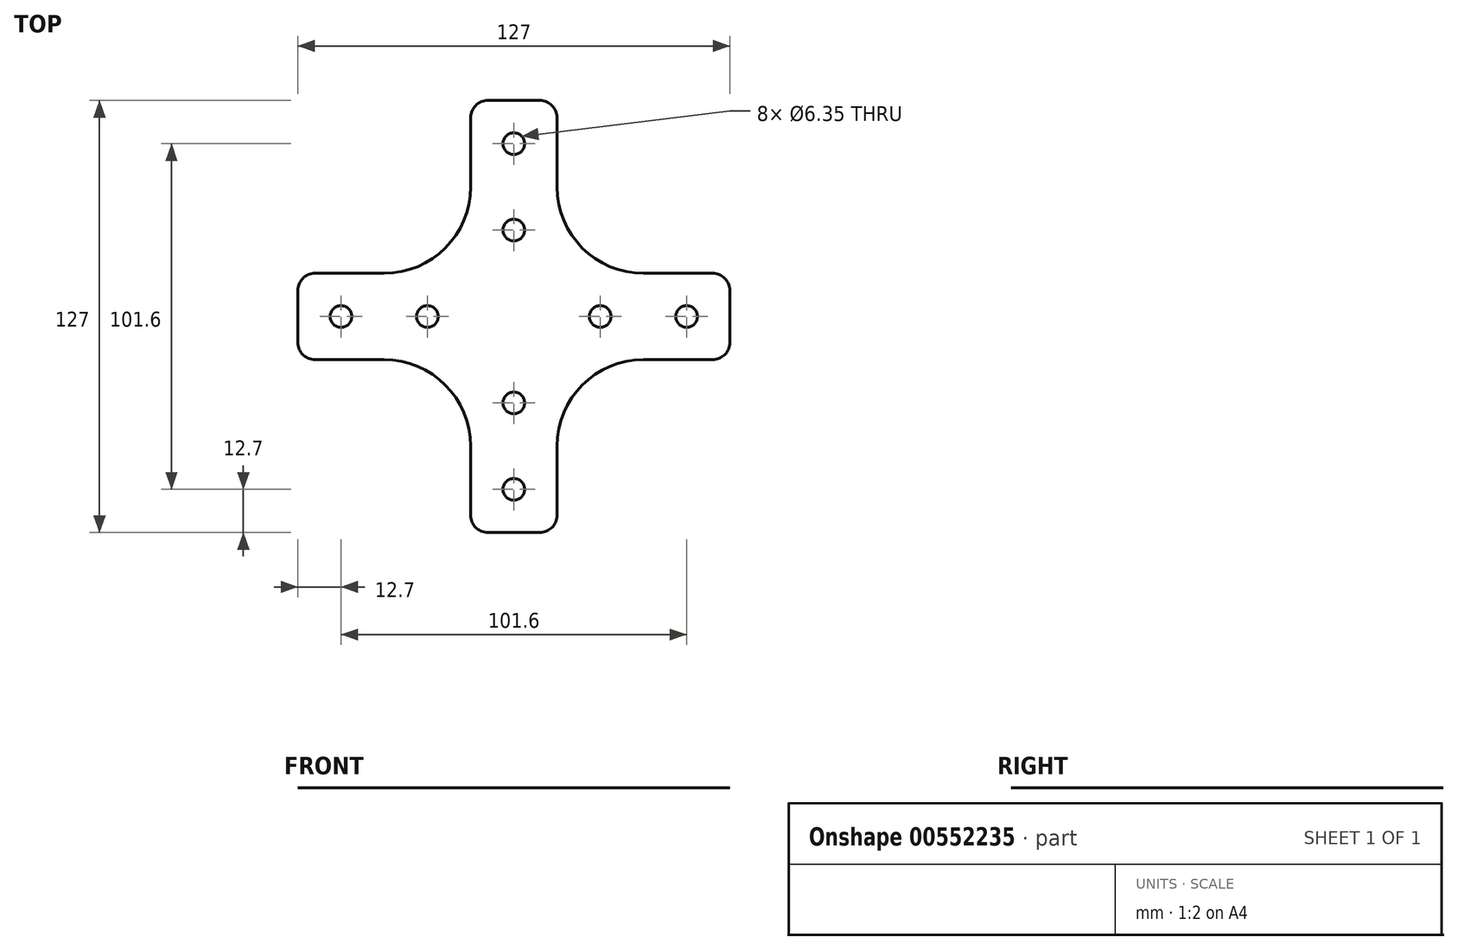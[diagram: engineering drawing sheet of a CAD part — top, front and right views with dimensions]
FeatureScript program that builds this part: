
annotation { "Feature Type Name" : "Feature", "Feature Type Description" : "" }
export const myFeature = defineFeature(function(context is Context, id is Id, definition is map)
    precondition{}
    {
        {
            var Q0;
            Q0=qCreatedBy(makeId("Top.planeOp"),FACE);
            var sketch = newSketch(context, id + "F0", { "sketchPlane" : qUnion([Q0])});
            skPoint(sketch, "E0.middle", {"position": v(0, 0) * mm});
            skLineSegment(sketch, "E1.bottom", {"start": v(-58.42, -12.7) * mm, "end": v(-38.1, -12.7) * mm});
            skLineSegment(sketch, "E1.top", {"start": v(-58.42, 12.7) * mm, "end": v(-38.1, 12.7) * mm});
            skLineSegment(sketch, "E2.left", {"start": v(-12.7, -58.42) * mm, "end": v(-12.7, -38.1) * mm});
            skLineSegment(sketch, "E2.right", {"start": v(12.7, -58.42) * mm, "end": v(12.7, -38.1) * mm});
            skLineSegment(sketch, "E3", {"start": v(38.1, -12.7) * mm, "end": v(58.42, -12.7) * mm});
            skLineSegment(sketch, "E4.bottom", {"start": v(-7.62, 63.5) * mm, "end": v(7.62, 63.5) * mm});
            skLineSegment(sketch, "E4.left", {"start": v(-12.7, 58.42) * mm, "end": v(-12.7, 38.1) * mm});
            skLineSegment(sketch, "E4.right", {"start": v(12.7, 58.42) * mm, "end": v(12.7, 38.1) * mm});
            skLineSegment(sketch, "E5.top", {"start": v(58.42, 12.7) * mm, "end": v(38.1, 12.7) * mm});
            skLineSegment(sketch, "E6.left", {"start": v(-63.5, 7.62) * mm, "end": v(-63.5, 0) * mm});
            skLineSegment(sketch, "E7.top", {"start": v(0, -63.5) * mm, "end": v(-7.62, -63.5) * mm});
            skLineSegment(sketch, "E8.right", {"start": v(63.5, 0) * mm, "end": v(63.5, -7.62) * mm});
            skCircle(sketch, "E9", {"center": v(-50.8, 0) * mm, "radius": 3.18 * mm});
            skCircle(sketch, "E10", {"center": v(-25.4, 0) * mm, "radius": 3.18 * mm});
            skCircle(sketch, "E11", {"center": v(0, -50.8) * mm, "radius": 3.18 * mm});
            skCircle(sketch, "E12", {"center": v(0, -25.4) * mm, "radius": 3.18 * mm});
            skCircle(sketch, "E13", {"center": v(50.8, 0) * mm, "radius": 3.18 * mm});
            skCircle(sketch, "E14", {"center": v(25.4, 0) * mm, "radius": 3.18 * mm});
            skCircle(sketch, "E15", {"center": v(0, 50.8) * mm, "radius": 3.18 * mm});
            skCircle(sketch, "E16", {"center": v(0, 25.4) * mm, "radius": 3.18 * mm});
            skArc(sketch, "E17.filletArc", {"start": v(-12.7, -38.1) * mm, "mid": v(-20.14, -20.14) * mm, "end": v(-38.1, -12.7) * mm});
            skArc(sketch, "E18.filletArc", {"start": v(38.1, -12.7) * mm, "mid": v(20.14, -20.14) * mm, "end": v(12.7, -38.1) * mm});
            skArc(sketch, "E19.filletArc", {"start": v(12.7, 38.1) * mm, "mid": v(20.14, 20.14) * mm, "end": v(38.1, 12.7) * mm});
            skArc(sketch, "E20.filletArc", {"start": v(-38.1, 12.7) * mm, "mid": v(-20.14, 20.14) * mm, "end": v(-12.7, 38.1) * mm});
            skArc(sketch, "E21.filletArc", {"start": v(-63.5, -7.62) * mm, "mid": v(-62.01, -11.21) * mm, "end": v(-58.42, -12.7) * mm});
            skArc(sketch, "E22.filletArc", {"start": v(-58.42, 12.7) * mm, "mid": v(-62.01, 11.21) * mm, "end": v(-63.5, 7.62) * mm});
            skArc(sketch, "E23.filletArc", {"start": v(-12.7, -58.42) * mm, "mid": v(-11.21, -62.01) * mm, "end": v(-7.62, -63.5) * mm});
            skArc(sketch, "E24.filletArc", {"start": v(7.62, -63.5) * mm, "mid": v(11.21, -62.01) * mm, "end": v(12.7, -58.42) * mm});
            skArc(sketch, "E25.filletArc", {"start": v(58.42, -12.7) * mm, "mid": v(62.01, -11.21) * mm, "end": v(63.5, -7.62) * mm});
            skArc(sketch, "E26.filletArc", {"start": v(63.5, 7.62) * mm, "mid": v(62.01, 11.21) * mm, "end": v(58.42, 12.7) * mm});
            skArc(sketch, "E27.filletArc", {"start": v(-7.62, 63.5) * mm, "mid": v(-11.21, 62.01) * mm, "end": v(-12.7, 58.42) * mm});
            skArc(sketch, "E28.filletArc", {"start": v(12.7, 58.42) * mm, "mid": v(11.21, 62.01) * mm, "end": v(7.62, 63.5) * mm});
            skLineSegment(sketch, "E29", {"start": v(-63.5, -7.62) * mm, "end": v(-63.5, 0) * mm});
            skLineSegment(sketch, "E30", {"start": v(7.62, -63.5) * mm, "end": v(0, -63.5) * mm});
            skLineSegment(sketch, "E31", {"start": v(63.5, 0) * mm, "end": v(63.5, 7.62) * mm});
            skSolve(sketch);
        }
        {
            var Q0;
            Q0 = qSketchRegion(id + "F0", true);
            extrude(context, id + "F1", {"entities" : qUnion([Q0]), "depth" : 1 / 203.2 * mm, "offsetDistance" : 25.4 * mm});
        }
    });
